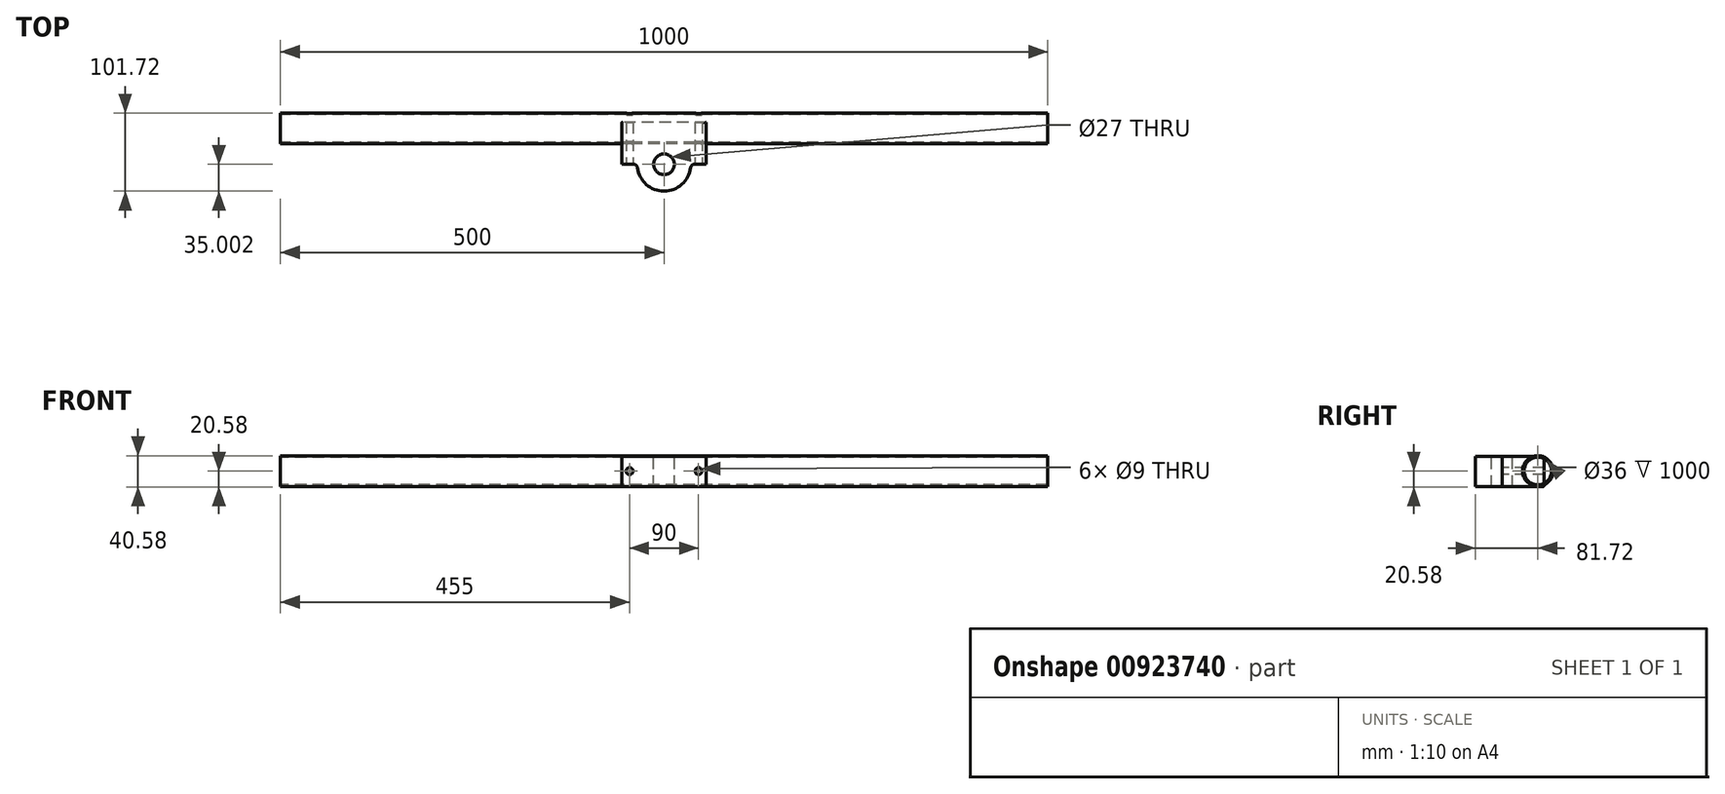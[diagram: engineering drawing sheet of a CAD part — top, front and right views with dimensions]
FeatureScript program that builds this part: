
annotation { "Feature Type Name" : "Feature", "Feature Type Description" : "" }
export const myFeature = defineFeature(function(context is Context, id is Id, definition is map)
    precondition{}
    {
        {
            var Q0;
            Q0=qCreatedBy(makeId("Right.planeOp"),FACE);
            var sketch = newSketch(context, id + "F0", { "sketchPlane" : qUnion([Q0]), "disableImprinting" : false});
            skCircle(sketch, "E0", {"center": v(0, 0) * mm, "radius": 20 * mm});
            skCircle(sketch, "E1.0", {"center": v(0, 0) * mm, "radius": 18 * mm});
            skSolve(sketch);
        }
        {
            var Q0;
            Q0 = qSketchRegion(id + "F0", true);
            extrude(context, id + "F1", {"entities" : qUnion([Q0]), "depth" : 1000 * mm, "offsetDistance" : 25 * mm, "symmetric" : true});
        }
        {
            var Q0;
            Q0=qCreatedBy(makeId("Right.planeOp"),FACE);
            var sketch = newSketch(context, id + "F2", { "sketchPlane" : qUnion([Q0]), "disableImprinting" : false});
            skLineSegment(sketch, "E2", {"start": v(8.28, -20.58) * mm, "end": v(8.28, 19.42) * mm});
            skLineSegment(sketch, "E3", {"start": v(8.28, 19.42) * mm, "end": v(-81.72, 19.42) * mm});
            skLineSegment(sketch, "E4", {"start": v(-81.72, 19.42) * mm, "end": v(-81.72, -20.58) * mm});
            skLineSegment(sketch, "E5", {"start": v(-81.72, -20.58) * mm, "end": v(8.28, -20.58) * mm});
            skSolve(sketch);
        }
        {
            var Q0;
            Q0 = qSketchRegion(id + "F2", true);
            extrude(context, id + "F3", {"entities" : qUnion([Q0]), "depth" : 110 * mm, "offsetDistance" : 25 * mm, "symmetric" : true});
        }
        {
            var Q0;
            Q0=makeQuery(id+"F3.opExtrude","SWEPT_FACE",FACE,{"disambiguationData":[OSD([sQuery(id+"F2.wireOp",EDGE,"E3")])]});
            var sketch = newSketch(context, id + "F4", { "sketchPlane" : qUnion([Q0]), "disableImprinting" : false});
            skLineSegment(sketch, "E6.0", {"start": v(-55, -46.72) * mm, "end": v(-55, -81.72) * mm});
            skLineSegment(sketch, "E7.0", {"start": v(55, -46.72) * mm, "end": v(55, -81.72) * mm});
            skLineSegment(sketch, "E8", {"start": v(-55, -46.72) * mm, "end": v(-35, -46.72) * mm});
            skArc(sketch, "E9", {"start": v(-35, -46.72) * mm, "mid": v(0, -81.72) * mm, "end": v(35, -46.72) * mm});
            skLineSegment(sketch, "E10", {"start": v(35, -46.72) * mm, "end": v(55, -46.72) * mm});
            skPoint(sketch, "E11.orphan", {"position": v(-55, 8.28) * mm});
            skPoint(sketch, "E12.orphan", {"position": v(55, 8.28) * mm});
            skCircle(sketch, "E13", {"center": v(0, -46.72) * mm, "radius": 13.5 * mm});
            skSolve(sketch);
        }
        {
            var Q0;
            Q0 = qSketchRegion(id + "F4", true);
            var Q1;
            {var subQ0=sQuery(id+"F4.wireOp",EDGE,"E7.0");Q1=makeQuery(id+"F4.imprint","IMPRINT",FACE,{"disambiguationData":[TD([[makeQuery(id+"F4.imprint","IMPRINT",EDGE,{"derivedFrom":subQ0}),-1.0]])]});}
            var Q2;
            {var subQ0=sQuery(id+"F4.wireOp",EDGE,"E6.0");Q2=makeQuery(id+"F4.imprint","IMPRINT",FACE,{"disambiguationData":[TD([[makeQuery(id+"F4.imprint","IMPRINT",EDGE,{"derivedFrom":subQ0}),1.0]])]});}
            extrude(context, id + "F5", {"entities" : qUnion([Q0, Q1, Q2]), "operationType" : NewBodyOperationType.REMOVE, "endBound" : BoundingType.THROUGH_ALL, "oppositeDirection" : true, "depth" : 25 * mm, "offsetDistance" : 25 * mm});
        }
        {
            var Q0;
            Q0=makeQuery(id+"F5.boolean.opBoolean","COPY",EDGE,{"derivedFrom":makeQuery(id+"F5.opExtrude","SWEPT_EDGE",EDGE,{"disambiguationData":[OSD([sQuery(id+"F4.wireOp",EDGE,"E9"),sQuery(id+"F4.wireOp",EDGE,"E10")])]})});
            var Q1;
            Q1=makeQuery(id+"F5.boolean.opBoolean","COPY",EDGE,{"derivedFrom":makeQuery(id+"F5.opExtrude","SWEPT_EDGE",EDGE,{"disambiguationData":[OSD([sQuery(id+"F2.wireOp",EDGE,"E3"),sQuery(id+"F4.wireOp",EDGE,"E7.0"),sQuery(id+"F4.wireOp",EDGE,"E10")])]})});
            var Q2;
            Q2=makeQuery(id+"F5.boolean.opBoolean","COPY",EDGE,{"derivedFrom":makeQuery(id+"F5.opExtrude","SWEPT_EDGE",EDGE,{"disambiguationData":[OSD([sQuery(id+"F2.wireOp",EDGE,"E3"),sQuery(id+"F4.wireOp",EDGE,"E6.0"),sQuery(id+"F4.wireOp",EDGE,"E8")])]})});
            var Q3;
            Q3=makeQuery(id+"F5.boolean.opBoolean","COPY",EDGE,{"derivedFrom":makeQuery(id+"F5.opExtrude","SWEPT_EDGE",EDGE,{"disambiguationData":[OSD([sQuery(id+"F4.wireOp",EDGE,"E8"),sQuery(id+"F4.wireOp",EDGE,"E9")])]})});
            fillet(context, id + "F6", {"entities" : qUnion([Q0, Q1, Q2, Q3]), "tangentPropagation" : true, "radius" : 5 * mm, "defaultsChanged" : false, "vertexSettings" : [], "allowEdgeOverflow" : false});
        }
        {
            var Q0;
            Q0=makeQuery(id+"F5.boolean.opBoolean","COPY",FACE,{"derivedFrom":makeQuery(id+"F5.opExtrude","SWEPT_FACE",FACE,{"disambiguationData":[OSD([sQuery(id+"F4.wireOp",EDGE,"E8")])]})});
            var sketch = newSketch(context, id + "F7", { "sketchPlane" : qUnion([Q0])});
            skCircle(sketch, "E14", {"center": v(-45, 0) * mm, "radius": 4.5 * mm});
            skCircle(sketch, "E15.1.0.0", {"center": v(45, 0) * mm, "radius": 4.5 * mm});
            skLineSegment(sketch, "E15.direction1", {"start": v(-45, 0) * mm, "end": v(45, 0) * mm, "construction": true});
            skSolve(sketch);
        }
        {
            var Q0;
            Q0 = qSketchRegion(id + "F7", true);
            extrude(context, id + "F8", {"entities" : qUnion([Q0]), "operationType" : NewBodyOperationType.REMOVE, "flatOperationType" : FlatOperationType.REMOVE, "thickness1" : 5 * mm, "thickness2" : 0 * mm, "endBound" : BoundingType.THROUGH_ALL, "oppositeDirection" : true, "depth" : 25 * mm, "offsetDistance" : 25 * mm, "startOffsetBound" : StartOffsetType.BLIND, "startOffsetDistance" : 25 * mm, "domain" : OperationDomain.MODEL});
        }
        {
            var Q0;
            Q0=makeQuery(id+"F3.opExtrude","SWEPT_EDGE",EDGE,{"disambiguationData":[OSD([sQuery(id+"F2.wireOp",EDGE,"E2"),sQuery(id+"F2.wireOp",EDGE,"E3")])]});
            var Q1;
            Q1=makeQuery(id+"F3.opExtrude","SWEPT_EDGE",EDGE,{"disambiguationData":[OSD([sQuery(id+"F2.wireOp",EDGE,"E5"),sQuery(id+"F2.wireOp",EDGE,"FGgDNANv-2lG2-2nwa-Lqix-LXMTOSNKBAt1")])]});
            var Q2;
            Q2=makeQuery(id+"F3.opExtrude","CAP_EDGE",EDGE,{"disambiguationData":[OSD([sQuery(id+"F2.wireOp",EDGE,"E3")])],"isStart":false});
            var Q3;
            Q3=makeQuery(id+"F3.opExtrude","CAP_EDGE",EDGE,{"disambiguationData":[OSD([sQuery(id+"F2.wireOp",EDGE,"E5")])],"isStart":false});
            fillet(context, id + "F9", {"entities" : qUnion([Q0, Q1, Q2, Q3]), "tangentPropagation" : true, "radius" : 2 * mm, "defaultsChanged" : false, "vertexSettings" : [], "allowEdgeOverflow" : false});
        }
    });
